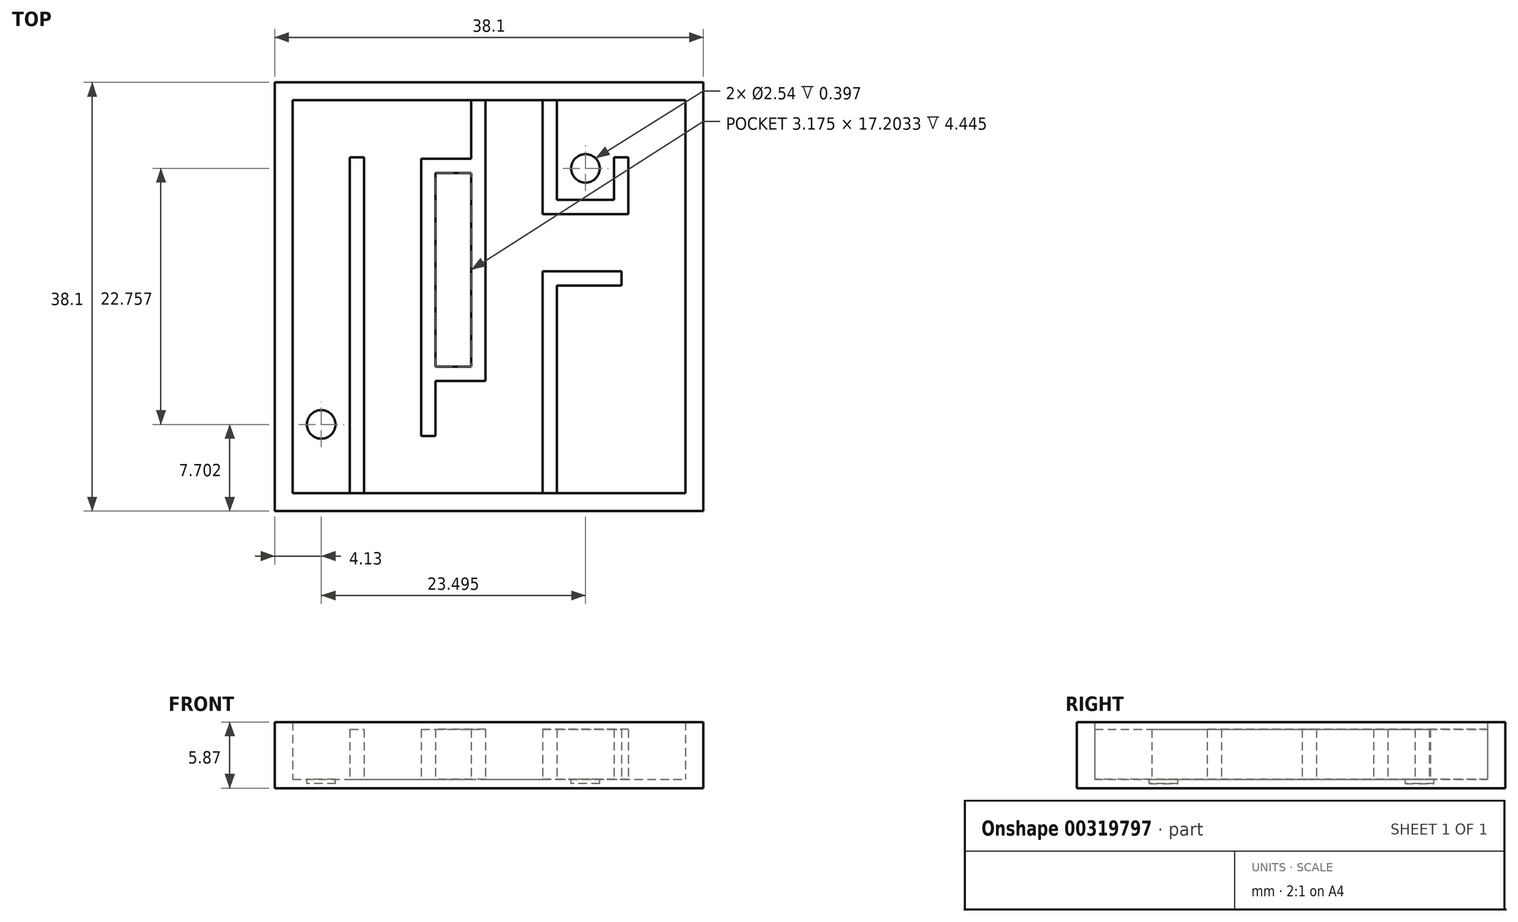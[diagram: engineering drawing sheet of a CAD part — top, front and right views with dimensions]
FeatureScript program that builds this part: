
annotation { "Feature Type Name" : "Feature", "Feature Type Description" : "" }
export const myFeature = defineFeature(function(context is Context, id is Id, definition is map)
    precondition{}
    {
        {
            var Q0;
            Q0=qCreatedBy(makeId("Top.planeOp"),FACE);
            var sketch = newSketch(context, id + "F0", { "sketchPlane" : qUnion([Q0])});
            skLineSegment(sketch, "E0.bottom", {"start": v(-20.75, 24.96) * mm, "end": v(17.35, 24.96) * mm});
            skLineSegment(sketch, "E0.top", {"start": v(-20.75, -13.14) * mm, "end": v(17.35, -13.14) * mm});
            skLineSegment(sketch, "E0.left", {"start": v(-20.75, 24.96) * mm, "end": v(-20.75, -13.14) * mm});
            skLineSegment(sketch, "E0.right", {"start": v(17.35, 24.96) * mm, "end": v(17.35, -13.14) * mm});
            skSolve(sketch);
        }
        {
            var Q0;
            Q0=makeQuery(id+"F0.imprint","IMPRINT",FACE,{"disambiguationData":[TD([[makeQuery(id+"F0.imprint","IMPRINT",EDGE,{"derivedFrom":sQuery(id+"F0.wireOp",EDGE,"E0.bottom")}),-1.0]])]});
            extrude(context, id + "F1", {"entities" : qUnion([Q0]), "depth" : 0.8 * mm});
        }
        {
            var Q0;
            Q0=makeQuery(id+"F1.opExtrude","CAP_FACE",FACE,{"disambiguationData":[OSD([sQuery(id+"F0.wireOp",EDGE,"E0.bottom"),sQuery(id+"F0.wireOp",EDGE,"E0.top"),sQuery(id+"F0.wireOp",EDGE,"E0.left"),sQuery(id+"F0.wireOp",EDGE,"E0.right")])],"isStart":false});
            var sketch = newSketch(context, id + "F2", { "sketchPlane" : qUnion([Q0])});
            skLineSegment(sketch, "E1.0", {"start": v(-19.16, 23.37) * mm, "end": v(15.76, 23.37) * mm});
            skLineSegment(sketch, "E1.1", {"start": v(-19.16, 23.37) * mm, "end": v(-19.16, -11.55) * mm});
            skLineSegment(sketch, "E1.2", {"start": v(-19.16, -11.55) * mm, "end": v(15.76, -11.55) * mm});
            skLineSegment(sketch, "E1.3", {"start": v(15.76, 23.37) * mm, "end": v(15.76, -11.55) * mm});
            skSolve(sketch);
        }
        {
            var Q0;
            Q0=makeQuery(id+"F2.imprint","IMPRINT",FACE,{"disambiguationData":[TD([[makeQuery(id+"F2.imprint","IMPRINT",EDGE,{"derivedFrom":sQuery(id+"F2.wireOp",EDGE,"E1.0")}),1.0]])]});
            extrude(context, id + "F3", {"entities" : qUnion([Q0]), "operationType" : NewBodyOperationType.ADD, "depth" : 5.08 * mm});
        }
        {
            var Q0;
            Q0=makeQuery(id+"F1.opExtrude","CAP_FACE",FACE,{"disambiguationData":[OSD([sQuery(id+"F0.wireOp",EDGE,"E0.bottom"),sQuery(id+"F0.wireOp",EDGE,"E0.top"),sQuery(id+"F0.wireOp",EDGE,"E0.left"),sQuery(id+"F0.wireOp",EDGE,"E0.right")])],"isStart":false});
            var sketch = newSketch(context, id + "F4", { "sketchPlane" : qUnion([Q0])});
            skLineSegment(sketch, "E2.bottom", {"start": v(-14.08, -11.55) * mm, "end": v(-12.81, -11.55) * mm});
            skLineSegment(sketch, "E2.top", {"start": v(-14.08, 18.3) * mm, "end": v(-12.81, 18.3) * mm});
            skLineSegment(sketch, "E2.left", {"start": v(-14.08, -11.55) * mm, "end": v(-14.08, 18.3) * mm});
            skLineSegment(sketch, "E2.right", {"start": v(-12.81, -11.55) * mm, "end": v(-12.81, 18.3) * mm});
            skLineSegment(sketch, "E3.bottom", {"start": v(-7.73, -6.47) * mm, "end": v(-6.46, -6.47) * mm});
            skLineSegment(sketch, "E3.top", {"start": v(-7.73, 18.18) * mm, "end": v(-6.46, 18.18) * mm});
            skLineSegment(sketch, "E3.left", {"start": v(-7.73, -6.47) * mm, "end": v(-7.73, 18.18) * mm});
            skLineSegment(sketch, "E3.right", {"start": v(-6.46, -6.47) * mm, "end": v(-6.46, -1.57) * mm});
            skLineSegment(sketch, "E4.top", {"start": v(-6.46, 16.9) * mm, "end": v(-3.29, 16.9) * mm});
            skLineSegment(sketch, "E4.right", {"start": v(-2.02, 18.18) * mm, "end": v(-2.02, 16.9) * mm});
            skLineSegment(sketch, "E5.top", {"start": v(3.39, 23.37) * mm, "end": v(-2.02, 23.37) * mm});
            skLineSegment(sketch, "E5.left", {"start": v(-2.02, 18.18) * mm, "end": v(-2.02, 23.37) * mm});
            skLineSegment(sketch, "E6", {"start": v(-6.46, 18.18) * mm, "end": v(-3.29, 18.18) * mm});
            skLineSegment(sketch, "E7", {"start": v(-3.29, 18.18) * mm, "end": v(-3.29, 23.37) * mm});
            skLineSegment(sketch, "E8", {"start": v(-3.29, 23.37) * mm, "end": v(-2.02, 23.37) * mm});
            skLineSegment(sketch, "E9.top", {"start": v(-2.02, -1.57) * mm, "end": v(-3.29, -1.57) * mm});
            skLineSegment(sketch, "E9.left", {"start": v(-2.02, 16.9) * mm, "end": v(-2.02, -1.57) * mm});
            skLineSegment(sketch, "E9.right", {"start": v(-3.29, 16.9) * mm, "end": v(-3.29, -0.3) * mm});
            skLineSegment(sketch, "E10.bottom", {"start": v(3.06, -11.55) * mm, "end": v(4.33, -11.55) * mm});
            skLineSegment(sketch, "E10.top", {"start": v(3.06, 8.16) * mm, "end": v(4.33, 8.16) * mm});
            skLineSegment(sketch, "E10.left", {"start": v(3.06, -11.55) * mm, "end": v(3.06, 8.16) * mm});
            skLineSegment(sketch, "E10.right", {"start": v(4.33, -11.55) * mm, "end": v(4.33, 6.9) * mm});
            skLineSegment(sketch, "E11.bottom", {"start": v(4.33, 23.37) * mm, "end": v(3.06, 23.37) * mm});
            skLineSegment(sketch, "E11.top", {"start": v(4.33, 13.24) * mm, "end": v(3.06, 13.24) * mm});
            skLineSegment(sketch, "E11.left", {"start": v(4.33, 23.37) * mm, "end": v(4.33, 14.51) * mm});
            skLineSegment(sketch, "E11.right", {"start": v(3.06, 23.37) * mm, "end": v(3.06, 13.24) * mm});
            skLineSegment(sketch, "E12.bottom", {"start": v(4.33, 13.24) * mm, "end": v(10.68, 13.24) * mm});
            skLineSegment(sketch, "E12.top", {"start": v(4.33, 14.51) * mm, "end": v(9.41, 14.51) * mm});
            skLineSegment(sketch, "E12.right", {"start": v(10.68, 13.24) * mm, "end": v(10.68, 14.51) * mm});
            skLineSegment(sketch, "E13.top", {"start": v(10.68, 18.3) * mm, "end": v(9.41, 18.3) * mm});
            skLineSegment(sketch, "E13.left", {"start": v(10.68, 14.51) * mm, "end": v(10.68, 18.3) * mm});
            skLineSegment(sketch, "E13.right", {"start": v(9.41, 14.51) * mm, "end": v(9.41, 18.3) * mm});
            skLineSegment(sketch, "E14.bottom", {"start": v(4.33, 8.16) * mm, "end": v(10.07, 8.16) * mm});
            skLineSegment(sketch, "E14.top", {"start": v(4.33, 6.9) * mm, "end": v(10.07, 6.9) * mm});
            skLineSegment(sketch, "E14.right", {"start": v(10.07, 8.16) * mm, "end": v(10.07, 6.9) * mm});
            skLineSegment(sketch, "E15", {"start": v(-19.16, -11.55) * mm, "end": v(-14.08, -11.55) * mm});
            skCircle(sketch, "E16", {"center": v(-16.62, -5.44) * mm, "radius": 1.27 * mm});
            skPoint(sketch, "E16.centerSnap0", {"position": v(-16.62, -11.55) * mm});
            skCircle(sketch, "E17", {"center": v(6.87, 17.32) * mm, "radius": 1.27 * mm});
            skPoint(sketch, "E17.centerSnap0", {"position": v(6.87, 14.51) * mm});
            skLineSegment(sketch, "E18.bottom", {"start": v(-3.29, -1.57) * mm, "end": v(-6.46, -1.57) * mm});
            skLineSegment(sketch, "E18.top", {"start": v(-3.29, -0.3) * mm, "end": v(-6.46, -0.3) * mm});
            skLineSegment(sketch, "E19.trimOffspring", {"start": v(-6.46, -0.3) * mm, "end": v(-6.46, 16.9) * mm});
            skSolve(sketch);
        }
        {
            var Q0;
            Q0=makeQuery(id+"F4.imprint","IMPRINT",FACE,{"disambiguationData":[TD([[makeQuery(id+"F4.imprint","IMPRINT",EDGE,{"derivedFrom":sQuery(id+"F4.wireOp",EDGE,"E16")}),1.0]])]});
            var Q1;
            Q1=makeQuery(id+"F4.imprint","IMPRINT",FACE,{"disambiguationData":[TD([[makeQuery(id+"F4.imprint","IMPRINT",EDGE,{"derivedFrom":sQuery(id+"F4.wireOp",EDGE,"E17")}),1.0]])]});
            extrude(context, id + "F5", {"entities" : qUnion([Q0, Q1]), "operationType" : NewBodyOperationType.REMOVE, "oppositeDirection" : true, "depth" : 0.4 * mm});
        }
        {
            var Q0;
            Q0=makeQuery(id+"F4.imprint","IMPRINT",FACE,{"disambiguationData":[TD([[makeQuery(id+"F4.imprint","IMPRINT",EDGE,{"derivedFrom":sQuery(id+"F4.wireOp",EDGE,"E2.bottom")}),1.0]])]});
            var Q1;
            Q1=makeQuery(id+"F4.imprint","IMPRINT",FACE,{"disambiguationData":[TD([[makeQuery(id+"F4.imprint","IMPRINT",EDGE,{"derivedFrom":sQuery(id+"F4.wireOp",EDGE,"E3.bottom")}),1.0]])]});
            var Q2;
            Q2=makeQuery(id+"F4.imprint","IMPRINT",FACE,{"disambiguationData":[TD([[makeQuery(id+"F4.imprint","IMPRINT",EDGE,{"derivedFrom":sQuery(id+"F4.wireOp",EDGE,"E10.bottom")}),1.0]])]});
            var Q3;
            Q3=makeQuery(id+"F4.imprint","IMPRINT",FACE,{"disambiguationData":[TD([[makeQuery(id+"F4.imprint","IMPRINT",EDGE,{"derivedFrom":sQuery(id+"F4.wireOp",EDGE,"E11.top")}),-1.0]])]});
            extrude(context, id + "F6", {"entities" : qUnion([Q0, Q1, Q2, Q3]), "operationType" : NewBodyOperationType.ADD, "depth" : 4.44 * mm});
        }
    });
